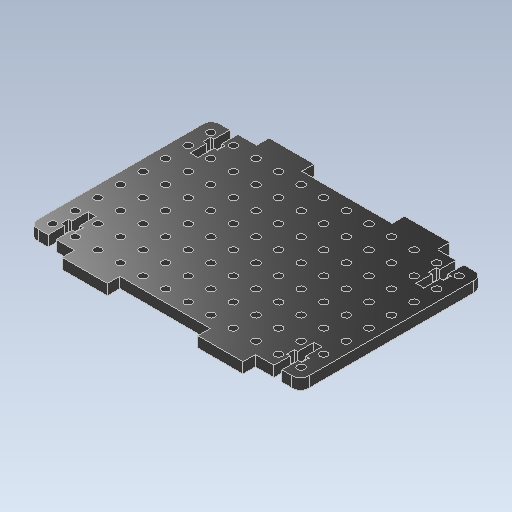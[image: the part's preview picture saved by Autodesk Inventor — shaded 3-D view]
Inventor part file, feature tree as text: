
AUTODESK INVENTOR PART (.ipt)
format: ipt  version: 2025 (Build 290162000, 162)  size: 322,560 bytes
history: native  units: mm
features: sketch x4, extrude x3, mirror x2, plane x1, fillet x1, hole x1, pattern_linear x1, projected_geometry x1
ambient origin geometry x8: Origin, YZ Plane, XZ Plane, XY Plane, X Axis, Y Axis, Z Axis, Center Point
bodies: Solid1 (feature_tree)
feature tree (14):
  extrude  "Extrusion1"  Depth=6.0mm
  plane  "Work Plane1"
  extrude  "Extrusion2"  Depth=6.0mm
  mirror  "Mirror1"
  extrude  "Extrusion3"  Depth=102.3mm
  fillet  "Fillet1"  Radius=7.0mm
  mirror  "Mirror2"
  hole  "Hole1"  [1 undecoded]
  pattern_linear  "Rectangular Pattern1"  Spacing1=0.0mm  [1 undecoded]
  sketch  "Sketch1"  dims[d1=6.0mm d2=0.0mm d3=6.7mm]
  sketch  "Sketch2"  dims[d4=4.25mm d5=6.0mm d6=4.0mm d7=2.0mm d8=90.0deg d9=8.0mm d10=20.594885mm d11=120.0mm d13=12.7mm d14=80.0mm d16=12.7mm]
  sketch  "Sketch3"  dims[d17=5.0mm d19=102.3mm d20=7.0mm]
  projected_geometry  "Projected Loop1"
  sketch  "Sketch4"  dims[d22=0.0mm d23=0.0mm d24=22.5mm d25=4.25mm d26=8.25mm d28=4.4958mm d29=0.0mm d30=0.0mm d31=152.4mm d32=76.2mm d33=25.4mm d44=127.0mm d45=6.35mm]
note: 2 required parameter values undecoded (feature->parameter linkage not recoverable at this tier; creation-order binding heuristic only, values carry confidence <= 0.55)
